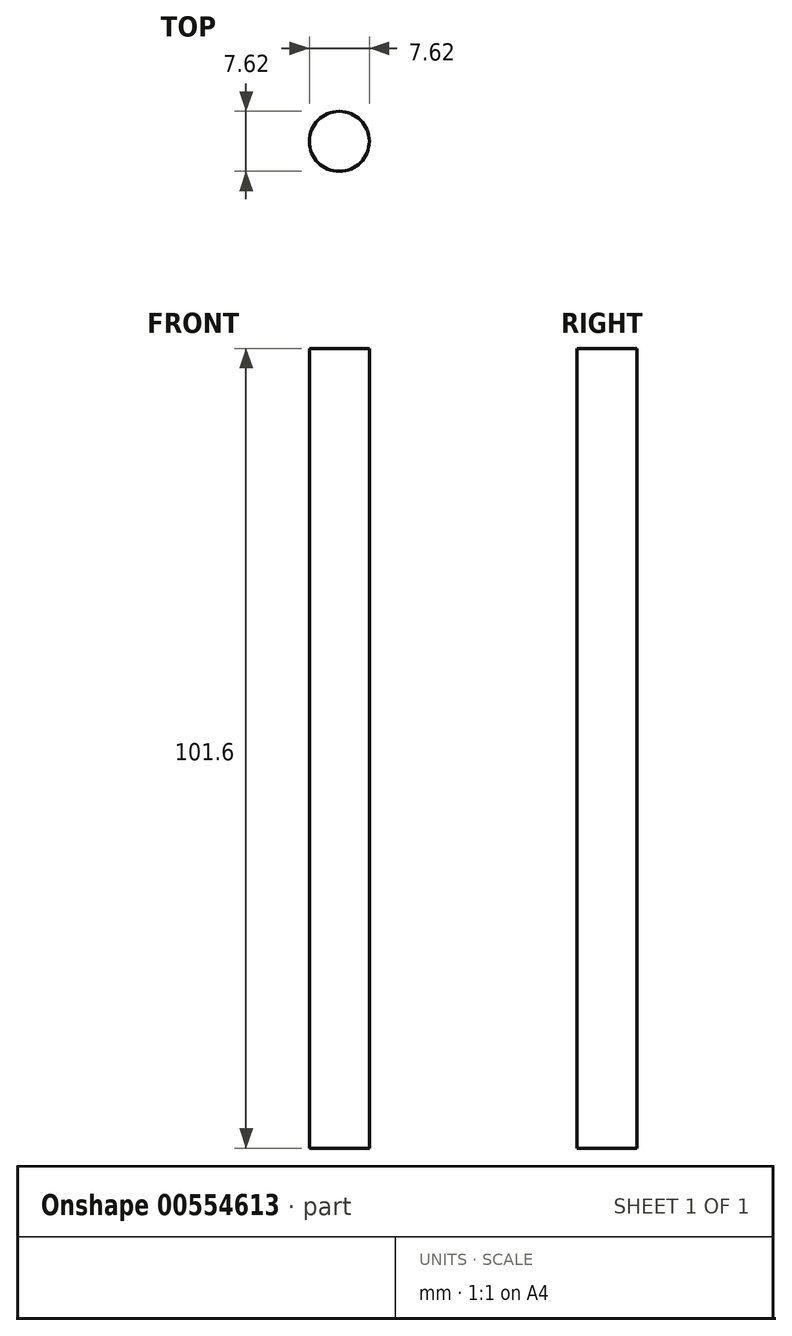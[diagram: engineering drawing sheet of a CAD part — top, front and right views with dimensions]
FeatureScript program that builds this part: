
annotation { "Feature Type Name" : "Feature", "Feature Type Description" : "" }
export const myFeature = defineFeature(function(context is Context, id is Id, definition is map)
    precondition{}
    {
        {
            var Q0;
            Q0=qCreatedBy(makeId("Top.planeOp"),FACE);
            var sketch = newSketch(context, id + "F0", { "sketchPlane" : qUnion([Q0])});
            skCircle(sketch, "E0", {"center": v(0, 0) * mm, "radius": 3.81 * mm});
            skSolve(sketch);
        }
        {
            var Q0;
            Q0=makeQuery(id+"F0.imprint","IMPRINT",FACE,{"disambiguationData":[TD([[makeQuery(id+"F0.imprint","IMPRINT",EDGE,{"derivedFrom":sQuery(id+"F0.wireOp",EDGE,"E0")}),1.0]])]});
            extrude(context, id + "F1", {"entities" : qUnion([Q0]), "depth" : 101.6 * mm, "offsetDistance" : 25.4 * mm});
        }
    });
